# Revit family: RBA2734-001
name_source: partatom
category: Plumbing Fixtures
units: mm (PartAtom-declared; Revit-internal decimal feet)

## family parameters
Cut with Voids When Loaded = Yes
Host = Face
OmniClass Number = 23.65.70.14.11
OmniClass Title = Drinking Fountains/Coolers
Part Type = Normal
Room Calculation Point = No
Round Connector Dimension = Use Diameter
Shared = Yes

## types (4) — shared parameters
-BF11 Bottle Filler with PushButton Operation = No
-BF12 Bottle Filler with Sensor Operation = No
-BF12-BAT Bottle Filler with Battery Operated Sensor Operation = No
-BF12-BCD Bottle Filler with Sensor Operation with Bottle Counter Display = No
-CSC5 Concealed Support Carrier = No
-DD Drop Down Door = No
-LOGO Customer Specified Logo / Graphics = No
-WF1 = No
-WF3 = No
120VAC/9.0VDC Plug-In Transformer = No
220V 220 Volt/50 Hz or 60 Hz Compressor = No
ADA Compliant = Yes
Activation = Push Button or Sensor Operated
Assembly Code = D2010820
BF = Bottle_Filler-Murdock-H2O-To-Go-BFI1-BF12_Series : BF11
BF11 = Bottle_Filler-Murdock-H2O-To-Go-BFI1-BF12_Series : BF11
BF12 = Bottle_Filler-Murdock-H2O-To-Go-BFI1-BF12_Series : BF12
BF12BAT = Bottle_Filler-Murdock-H2O-To-Go-BFI1-BF12_Series : BF12-BAT
BF12BCD = Bottle_Filler-Murdock-H2O-To-Go-BFI1-BF12_Series : BF12-BCD
Bottle Filler Type = Bottle_Filler-Murdock-H2O-To-Go-BFI1-BF12_Series : BF11
CW Connection = Yes
CWFU = 1.5
Cold Water Connection Diameter = 10 mm  [stored 0.0328084 ft]
Cold Water Connection Height = 492 mm
Cold Water Connection Width = 51 mm
Description = Barrier-Free, Wall Mount Drinking Fountain with Vandal Resistant Button and H2O to go!® Deck Mount Sensor Activated Bottle Filler
Fill Rate = 1 GPM Fill Rate
Finish = Stainless Steel-Murdock-Type 304-Satin
Finish- Bottle Filler Housing = Stainless Steel-Murdock-20 Gauge-Satin
Finish- Push Button = Brass-Murdock-Chrome Plated
Finish- Sensor = Plastic-Murdock-Black
Flow Rate = 0.3 GPM flow
Full Load Amps = 4.4
HW Connection = No
Height = 978 mm
Height From Floor Level = 838 mm
IAPMO Compliance = NSF/ANSI 61 & Federal Public Law 111-380 (No lead)
Installation Type = Wall Mounted
Laminar (LAM) = Yes
Length = 470 mm
Manufacturer = Murdock Manufacturing
Material = Stainless Steel-Murdock-Type 304-Satin
Maximum Run Time = 20 Seconds
Price = Prices may vary. Please consult Manufacturer Representative for most up-to-date price list.
Rated Watts = 335
URL = https://www.murdockmfg.com
Vent Connection = No
Voltage Nominal = 120 V
WFU = 2
Waste Connection = Yes
Waste Connection Diameter = 32 mm
Waste Connection Height = 565 mm
Water Pressure = 20-105 PSIG
Width = 470 mm
cUPC Compliant = Yes
zero-valued in all types: Default Elevation, HWFU

## per-type parameters (varying)
| type | Finish- Bubbler | Finish- Cabinet |
| A171108F-UG-BF | Silicone-Murdock-Grey | Galvanized Steel-Murdock-Powder Coat-Grey |
| A171408F-UG-BF | Silicone-Murdock-Grey | Stainless Steel-Murdock-Type 304-Satin |
| A171108S-UG-BF | Stainless Steel-Murdock-Polished | Galvanized Steel-Murdock-Powder Coat-Grey |
| A171408S-UG-BF | Stainless Steel-Murdock-Polished | Stainless Steel-Murdock-Type 304-Satin |

note: column(s) folded — value = type name in every type: Model

note: [stored X ft] marks values corroborated as IEEE doubles in the binary element streams (Revit-internal decimal feet)

## geometry (parser evidence)
native form markers: Sweep x5
no freeform markers — native parametric forms only
